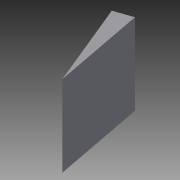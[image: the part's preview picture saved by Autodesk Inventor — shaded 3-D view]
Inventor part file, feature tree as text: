
AUTODESK INVENTOR PART (.ipt)
format: ipt  version: 2014 (Build 180170000, 170)  size: 68,608 bytes
history: native  units: in
note: dims shown in document units (in); Inventor stores cm internally (conversion verified against a paired STEP export)
features: extrude x1, sketch x1
ambient origin geometry x8: Origin, YZ Plane, XZ Plane, XY Plane, X Axis, Y Axis, Z Axis, Center Point
bodies: Solid1 (feature_tree)
feature tree (2):
  extrude  "Extrusion1"  Depth=32.5in
  sketch  "Sketch1"  dims[d2=0.5635in d3=36.12in d4=6.92in d5=33.75in d6=32.5in d7=0.0in]
